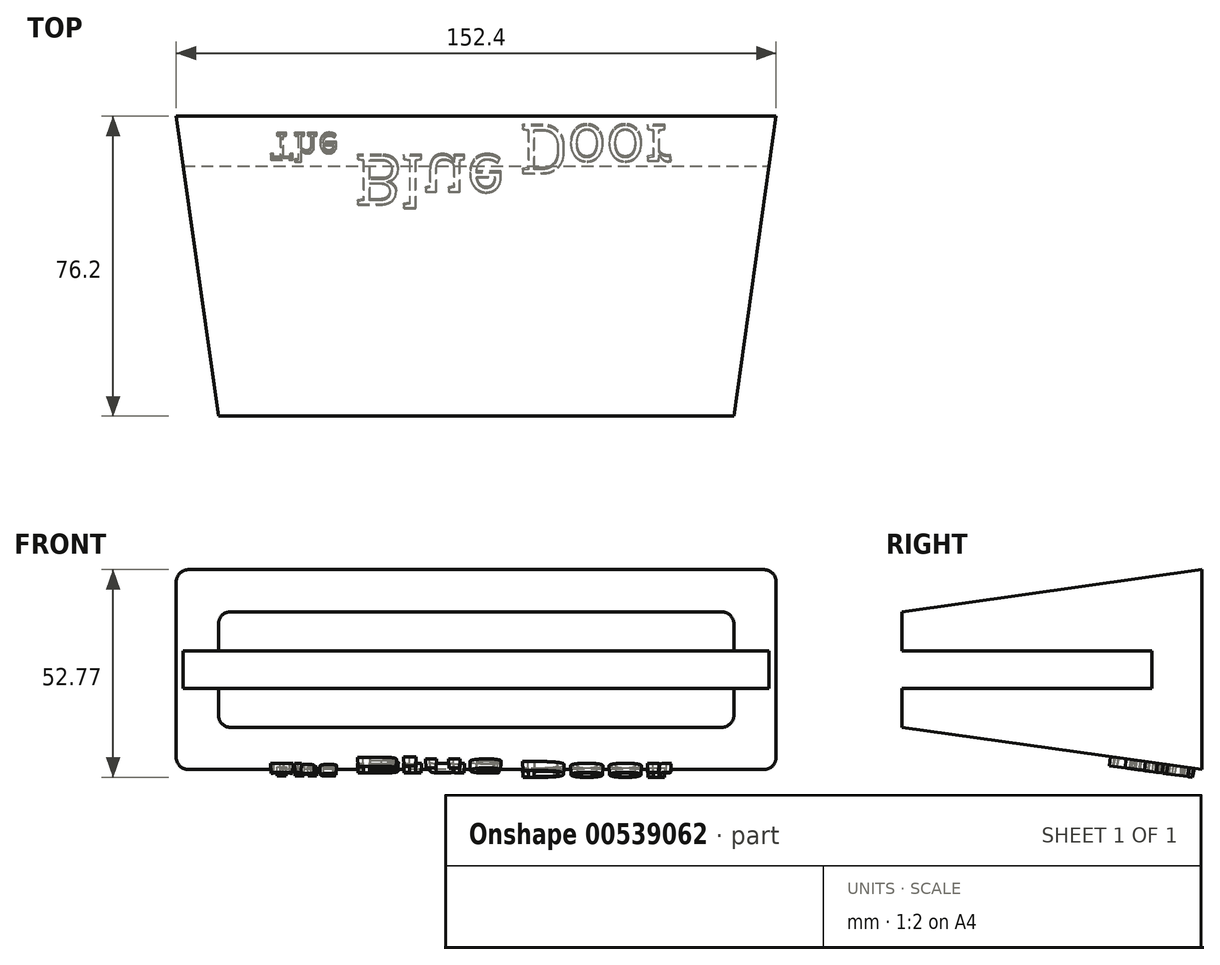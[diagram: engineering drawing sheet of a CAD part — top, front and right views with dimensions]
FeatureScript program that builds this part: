
annotation { "Feature Type Name" : "Feature", "Feature Type Description" : "" }
export const myFeature = defineFeature(function(context is Context, id is Id, definition is map)
    precondition{}
    {
        {
            var Q0;
            Q0=qCreatedBy(makeId("Front.planeOp"),FACE);
            var sketch = newSketch(context, id + "F0", { "sketchPlane" : qUnion([Q0])});
            skLineSegment(sketch, "E0.bottom", {"start": v(76.2, 25.4) * mm, "end": v(-76.2, 25.4) * mm});
            skLineSegment(sketch, "E0.top", {"start": v(76.2, -25.4) * mm, "end": v(-76.2, -25.4) * mm});
            skLineSegment(sketch, "E0.left", {"start": v(76.2, 25.4) * mm, "end": v(76.2, -25.4) * mm});
            skLineSegment(sketch, "E0.right", {"start": v(-76.2, 25.4) * mm, "end": v(-76.2, -25.4) * mm});
            skPoint(sketch, "E0.middle", {"position": v(0, 0) * mm});
            skSolve(sketch);
        }
        {
            var Q0;
            Q0=makeQuery(id+"F0.imprint","IMPRINT",FACE,{"disambiguationData":[TD([[makeQuery(id+"F0.imprint","IMPRINT",EDGE,{"derivedFrom":sQuery(id+"F0.wireOp",EDGE,"E0.bottom")}),1.0]])]});
            extrude(context, id + "F1", {"entities" : qUnion([Q0]), "depth" : 76.2 * mm, "offsetDistance" : 25.4 * mm, "hasDraft" : true, "draftAngle" : 8 * degree, "draftPullDirection" : true});
        }
        {
            var Q0;
            Q0=makeQuery(id+"F1.opExtrude","CAP_FACE",FACE,{"disambiguationData":[OSD([sQuery(id+"F0.wireOp",EDGE,"E0.bottom"),sQuery(id+"F0.wireOp",EDGE,"E0.top"),sQuery(id+"F0.wireOp",EDGE,"E0.left"),sQuery(id+"F0.wireOp",EDGE,"E0.right")])],"isStart":false});
            var sketch = newSketch(context, id + "F2", { "sketchPlane" : qUnion([Q0])});
            skLineSegment(sketch, "E1.bottom", {"start": v(-76.2, 4.76) * mm, "end": v(76.2, 4.76) * mm});
            skLineSegment(sketch, "E1.top", {"start": v(-76.2, -4.76) * mm, "end": v(76.2, -4.76) * mm});
            skLineSegment(sketch, "E1.left", {"start": v(-76.2, 4.76) * mm, "end": v(-76.2, -4.76) * mm});
            skLineSegment(sketch, "E1.right", {"start": v(76.2, 4.76) * mm, "end": v(76.2, -4.76) * mm});
            skLineSegment(sketch, "E2", {"start": v(0, 0) * mm, "end": v(-76.2, 0) * mm, "construction": true});
            skSolve(sketch);
        }
        {
            var Q0;
            Q0=makeQuery(id+"F2.imprint","IMPRINT",FACE,{"disambiguationData":[TD([[makeQuery(id+"F2.imprint","IMPRINT",EDGE,{"derivedFrom":sQuery(id+"F2.wireOp",EDGE,"E1.bottom")}),-1.0]])]});
            extrude(context, id + "F3", {"entities" : qUnion([Q0]), "operationType" : NewBodyOperationType.REMOVE, "oppositeDirection" : true, "depth" : 63.5 * mm, "offsetDistance" : 25.4 * mm});
        }
        {
            var Q0;
            Q0=makeQuery(id+"F1.opExtrude","SWEPT_EDGE",EDGE,{"disambiguationData":[OSD([sQuery(id+"F0.wireOp",EDGE,"E0.top"),sQuery(id+"F0.wireOp",EDGE,"E0.right")])]});
            var Q1;
            Q1=makeQuery(id+"F1.opExtrude","SWEPT_EDGE",EDGE,{"disambiguationData":[OSD([sQuery(id+"F0.wireOp",EDGE,"E0.bottom"),sQuery(id+"F0.wireOp",EDGE,"E0.left")])]});
            var Q2;
            Q2=makeQuery(id+"F1.opExtrude","SWEPT_EDGE",EDGE,{"disambiguationData":[OSD([sQuery(id+"F0.wireOp",EDGE,"E0.top"),sQuery(id+"F0.wireOp",EDGE,"E0.left")])]});
            var Q3;
            Q3=makeQuery(id+"F1.opExtrude","SWEPT_EDGE",EDGE,{"disambiguationData":[OSD([sQuery(id+"F0.wireOp",EDGE,"E0.bottom"),sQuery(id+"F0.wireOp",EDGE,"E0.right")])]});
            fillet(context, id + "F4", {"entities" : qUnion([Q0, Q1, Q2, Q3]), "radius" : 3.17 * mm, "tangentPropagation" : true, "allowEdgeOverflow" : false});
        }
        {
            var Q0;
            Q0=makeQuery(id+"F1.opExtrude","SWEPT_FACE",FACE,{"disambiguationData":[OSD([sQuery(id+"F0.wireOp",EDGE,"E0.top")])]});
            var sketch = newSketch(context, id + "F5", { "sketchPlane" : qUnion([Q0])});
            skText(sketch, "E3", { "text": "The", "fontName": "RobotoSlab-Regular.ttf"});
            skText(sketch, "E4", { "text": "Blue", "fontName": "RobotoSlab-Regular.ttf"});
            skText(sketch, "E5", { "text": "Door", "fontName": "RobotoSlab-Regular.ttf"});
            const initialGuessF5  = {"E3": [-0.05244, 0.0007, 1, 0, 0.00697], "E4": [-0.03076, 0.00626, 1, 0, 0.01294], "E5": [0.01118, -0.00138, 1, 0, 0.01253]};
            skSetInitialGuess(sketch, initialGuessF5);
            skSolve(sketch);
        }
        {
            var Q0;
            Q0 = qSketchRegion(id + "F5", true);
            extrude(context, id + "F6", {"entities" : qUnion([Q0]), "operationType" : NewBodyOperationType.ADD, "depth" : 2.3 * mm, "offsetDistance" : 25.4 * mm, "hasDraft" : true, "draftAngle" : 3 * degree, "draftPullDirection" : true});
        }
        {
            var Q0;
            Q0=qCreatedBy(makeId("Top.planeOp"),FACE);
            var sketch = newSketch(context, id + "F7", { "sketchPlane" : qUnion([Q0])});
            skLineSegment(sketch, "E6", {"start": v(0, 0) * mm, "end": v(0, -48.84) * mm, "construction": true});
            skSolve(sketch);
        }
    });
